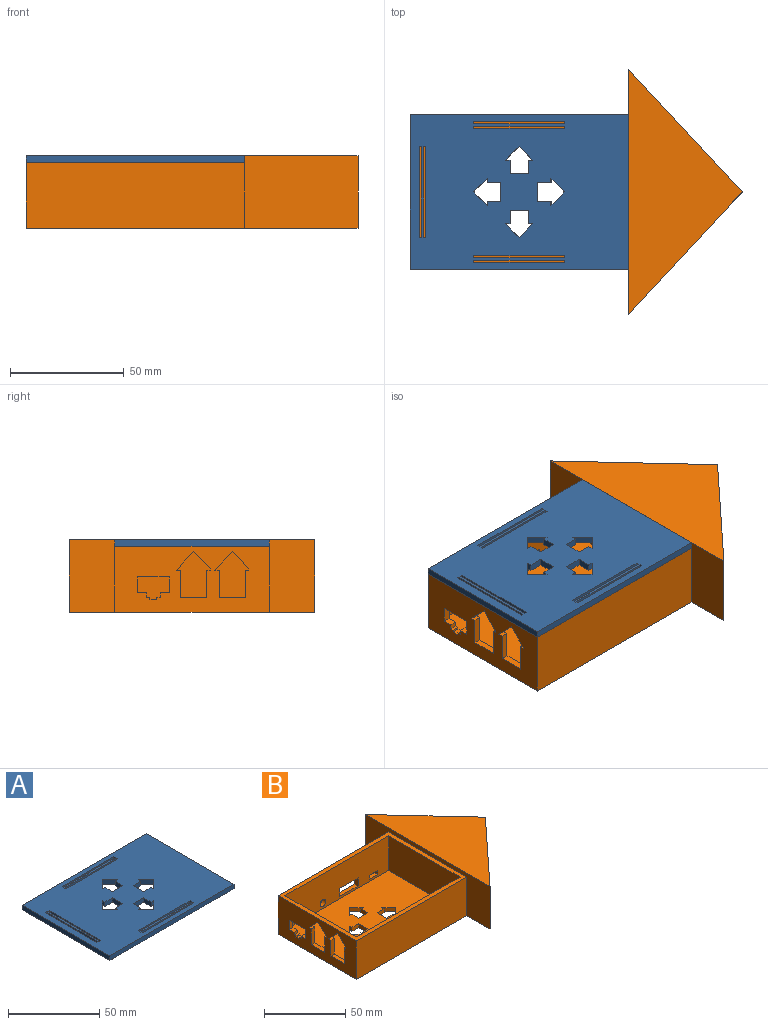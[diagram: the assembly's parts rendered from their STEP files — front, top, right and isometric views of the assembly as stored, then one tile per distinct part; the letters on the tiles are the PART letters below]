
ASSEMBLY  parts=2 mates=1
PART A: 86 faces, bbox 96x68x6 mm
  f0: plane 96x68mm, normal (0,0,-1), area 5872mm2, adj f2,f3,f4,f5,f6,f7,f8,f9
  f1: plane 96x68mm, normal (0,0,1), area 5952mm2, adj f2,f3,f4,f5,f34,f35,f36,f37
  f2: plane 68x3mm, normal (-1,0,0), area 204mm2, adj f0,f1,f3,f5
  f3: plane 96x3mm, normal (0,-1,0), area 288mm2, adj f0,f1,f2,f4
  f4: plane 68x3mm, normal (1,0,0), area 204mm2, adj f0,f1,f3,f5
  f5: plane 96x3mm, normal (0,1,0), area 288mm2, adj f0,f1,f2,f4
  f6: plane 6x3mm, normal (1,0,0), area 18mm2, adj f0,f7,f11,f12
  f7: plane 6x3mm, normal (0,-1,0), area 18mm2, adj f0,f6,f8,f12
  f8: plane 3x2mm, normal (-1,0,0), area 6mm2, adj f0,f7,f9,f12
  f9: plane 4x3mm, normal (0,1,0), area 12mm2, adj f0,f8,f10,f12
  f10: plane 4x3mm, normal (-1,0,0), area 12mm2, adj f0,f9,f11,f12
  f11: plane 3x2mm, normal (0,1,0), area 6mm2, adj f0,f6,f10,f12
  f12: plane 6x6mm, normal (0,0,-1), area 20mm2, adj f6,f7,f8,f9,f10,f11
  f13: plane 6x3mm, normal (1,0,0), area 18mm2, adj f0,f14,f18,f19
  f14: plane 3x2mm, normal (0,-1,0), area 6mm2, adj f0,f13,f15,f19
  f15: plane 4x3mm, normal (-1,0,0), area 12mm2, adj f0,f14,f16,f19
  f16: plane 4x3mm, normal (0,-1,0), area 12mm2, adj f0,f15,f17,f19
  f17: plane 3x2mm, normal (-1,0,0), area 6mm2, adj f0,f16,f18,f19
  f18: plane 6x3mm, normal (0,1,0), area 18mm2, adj f0,f13,f17,f19
  f19: plane 6x6mm, normal (0,0,-1), area 20mm2, adj f13,f14,f15,f16,f17,f18
  f20: plane 6x3mm, normal (0,-1,0), area 18mm2, adj f0,f21,f25,f26
  f21: plane 6x3mm, normal (-1,0,0), area 18mm2, adj f0,f20,f22,f26
  f22: plane 3x2mm, normal (0,1,0), area 6mm2, adj f0,f21,f23,f26
  f23: plane 4x3mm, normal (1,0,0), area 12mm2, adj f0,f22,f24,f26
  f24: plane 4x3mm, normal (0,1,0), area 12mm2, adj f0,f23,f25,f26
  f25: plane 3x2mm, normal (1,0,0), area 6mm2, adj f0,f20,f24,f26
  f26: plane 6x6mm, normal (0,0,-1), area 20mm2, adj f20,f21,f22,f23,f24,f25
  f27: plane 3x2mm, normal (0,-1,0), area 6mm2, adj f0,f28,f32,f33
  f28: plane 6x3mm, normal (-1,0,0), area 18mm2, adj f0,f27,f29,f33
  f29: plane 6x3mm, normal (0,1,0), area 18mm2, adj f0,f28,f30,f33
  f30: plane 3x2mm, normal (1,0,0), area 6mm2, adj f0,f29,f31,f33
  f31: plane 4x3mm, normal (0,-1,0), area 12mm2, adj f0,f30,f32,f33
  f32: plane 4x3mm, normal (1,0,0), area 12mm2, adj f0,f27,f31,f33
  f33: plane 6x6mm, normal (0,0,-1), area 20mm2, adj f27,f28,f29,f30,f31,f32
  f34: plane 8x3mm, normal (1,0,0), area 24mm2, adj f0,f1,f35,f40
  f35: plane 6x3mm, normal (0,1,0), area 18mm2, adj f0,f1,f34,f36
  f36: plane 3x2mm, normal (1,0,0), area 6mm2, adj f0,f1,f35,f37
  f37: plane 6x6mm, normal (-0.71,0.71,0), area 25.5mm2, adj f0,f1,f36,f38
  f38: plane 6x6mm, normal (-0.71,-0.71,0), area 25.5mm2, adj f0,f1,f37,f39
  f39: plane 3x2mm, normal (1,0,0), area 6mm2, adj f0,f1,f38,f40
  f40: plane 6x3mm, normal (0,-1,0), area 18mm2, adj f0,f1,f34,f39
  f41: plane 40x3mm, normal (0,1,0), area 120mm2, adj f0,f1,f42,f44
  f42: plane 3x1mm, normal (-1,0,0), area 3mm2, adj f0,f1,f41,f43
  f43: plane 40x3mm, normal (0,-1,0), area 120mm2, adj f0,f1,f42,f44
  f44: plane 3x1mm, normal (1,0,0), area 3mm2, adj f0,f1,f41,f43
  f45: plane 8x3mm, normal (0,-1,0), area 24mm2, adj f0,f1,f46,f51
  f46: plane 6x3mm, normal (1,0,0), area 18mm2, adj f0,f1,f45,f47
  f47: plane 3x2mm, normal (0,-1,0), area 6mm2, adj f0,f1,f46,f48
  f48: plane 6x6mm, normal (0.71,0.71,0), area 25.5mm2, adj f0,f1,f47,f49
  f49: plane 6x6mm, normal (-0.71,0.71,0), area 25.5mm2, adj f0,f1,f48,f50
  f50: plane 3x2mm, normal (0,-1,0), area 6mm2, adj f0,f1,f49,f51
  f51: plane 6x3mm, normal (-1,0,0), area 18mm2, adj f0,f1,f45,f50
  f52: plane 8x3mm, normal (-1,0,0), area 24mm2, adj f0,f1,f53,f58
  f53: plane 6x3mm, normal (0,-1,0), area 18mm2, adj f0,f1,f52,f54
  f54: plane 3x2mm, normal (-1,0,0), area 6mm2, adj f0,f1,f53,f55
  f55: plane 6x6mm, normal (0.71,-0.71,0), area 25.5mm2, adj f0,f1,f54,f56
  f56: plane 6x6mm, normal (0.71,0.71,0), area 25.5mm2, adj f0,f1,f55,f57
  f57: plane 3x2mm, normal (-1,0,0), area 6mm2, adj f0,f1,f56,f58
  f58: plane 6x3mm, normal (0,1,0), area 18mm2, adj f0,f1,f52,f57
  f59: plane 40x3mm, normal (1,0,0), area 120mm2, adj f0,f1,f60,f62
  f60: plane 3x1mm, normal (0,1,0), area 3mm2, adj f0,f1,f59,f61
  f61: plane 40x3mm, normal (-1,0,0), area 120mm2, adj f0,f1,f60,f62
  f62: plane 3x1mm, normal (0,-1,0), area 3mm2, adj f0,f1,f59,f61
  f63: plane 3x1mm, normal (0,1,0), area 3mm2, adj f0,f1,f64,f66
  f64: plane 40x3mm, normal (-1,0,0), area 120mm2, adj f0,f1,f63,f65
  f65: plane 3x1mm, normal (0,-1,0), area 3mm2, adj f0,f1,f64,f66
  f66: plane 40x3mm, normal (1,0,0), area 120mm2, adj f0,f1,f63,f65
  f67: plane 40x3mm, normal (0,-1,0), area 120mm2, adj f0,f1,f68,f70
  f68: plane 3x1mm, normal (1,0,0), area 3mm2, adj f0,f1,f67,f69
  f69: plane 40x3mm, normal (0,1,0), area 120mm2, adj f0,f1,f68,f70
  f70: plane 3x1mm, normal (-1,0,0), area 3mm2, adj f0,f1,f67,f69
  f71: plane 3x1mm, normal (-1,0,0), area 3mm2, adj f0,f1,f72,f74
  f72: plane 40x3mm, normal (0,-1,0), area 120mm2, adj f0,f1,f71,f73
  f73: plane 3x1mm, normal (1,0,0), area 3mm2, adj f0,f1,f72,f74
  f74: plane 40x3mm, normal (0,1,0), area 120mm2, adj f0,f1,f71,f73
  f75: plane 8x3mm, normal (0,1,0), area 24mm2, adj f0,f1,f76,f81
  f76: plane 6x3mm, normal (-1,0,0), area 18mm2, adj f0,f1,f75,f77
  f77: plane 3x2mm, normal (0,1,0), area 6mm2, adj f0,f1,f76,f78
  f78: plane 6x6mm, normal (-0.71,-0.71,0), area 25.5mm2, adj f0,f1,f77,f79
  f79: plane 6x6mm, normal (0.71,-0.71,0), area 25.5mm2, adj f0,f1,f78,f80
  f80: plane 3x2mm, normal (0,1,0), area 6mm2, adj f0,f1,f79,f81
  f81: plane 6x3mm, normal (1,0,0), area 18mm2, adj f0,f1,f75,f80
  f82: plane 3x1mm, normal (1,0,0), area 3mm2, adj f0,f1,f83,f85
  f83: plane 40x3mm, normal (0,1,0), area 120mm2, adj f0,f1,f82,f84
  f84: plane 3x1mm, normal (-1,0,0), area 3mm2, adj f0,f1,f83,f85
  f85: plane 40x3mm, normal (0,-1,0), area 120mm2, adj f0,f1,f82,f84
PART B: 79 faces, bbox 146x108x32 mm
  f0: plane 146x108mm, normal (0,0,-1), area 8892mm2, adj f1,f3,f5,f47,f48,f49,f51,f52
  f1: plane 96x29mm, normal (0,1,0), area 2647.4mm2, adj f0,f3,f8,f38,f39,f40,f41,f42
  f2: plane 90x26mm, normal (0,-1,0), area 2203.4mm2, adj f4,f6,f8,f9,f38,f39,f40,f41
  f3: plane 68x29mm, normal (-1,0,0), area 1459.3mm2, adj f0,f1,f5,f8,f10,f11,f12,f13
  f4: plane 62x26mm, normal (1,0,0), area 1099.3mm2, adj f2,f7,f8,f9,f10,f11,f12,f13
  f5: plane 96x29mm, normal (0,-1,0), area 2784mm2, adj f0,f3,f8,f47
  f6: plane 62x26mm, normal (-1,0,0), area 1612mm2, adj f2,f7,f8,f9
  f7: plane 90x26mm, normal (0,1,0), area 2340mm2, adj f4,f6,f8,f9
  f8: plane 96x68mm, normal (0,0,1), area 948mm2, adj f1,f2,f3,f4,f5,f6,f7,f47
  f9: plane 90x62mm, normal (0,0,1), area 5244mm2, adj f2,f4,f6,f7,f51,f52,f53,f54
  f10: plane 7.48x7.25mm, normal (0,0.72,-0.7), area 31.3mm2, adj f3,f4,f11,f17
  f11: plane 8x7.75mm, normal (0,-0.72,-0.7), area 33.4mm2, adj f3,f4,f10,f12
  f12: plane 3x2mm, normal (0,0,1), area 6mm2, adj f3,f4,f11,f13
  f13: plane 12x3mm, normal (0,-1,0), area 36mm2, adj f3,f4,f12,f14
  f14: plane 11.5x3mm, normal (0,0,1), area 34.5mm2, adj f3,f4,f13,f15
  f15: plane 12x3mm, normal (0,1,0), area 36mm2, adj f3,f4,f14,f16
  f16: plane 3x1.5mm, normal (0,0,1), area 4.5mm2, adj f3,f4,f15,f17
  f17: plane 3x0.52mm, normal (0,1,0), area 1.5mm2, adj f3,f4,f10,f16
  f18: plane 12x3mm, normal (0,1,0), area 36mm2, adj f3,f4,f19,f25
  f19: plane 3x1.5mm, normal (0,0,1), area 4.5mm2, adj f3,f4,f18,f20
  f20: plane 3x0.52mm, normal (0,1,0), area 1.5mm2, adj f3,f4,f19,f21
  f21: plane 7.48x7.25mm, normal (0,0.72,-0.7), area 31.3mm2, adj f3,f4,f20,f22
  f22: plane 8x7.75mm, normal (0,-0.72,-0.7), area 33.4mm2, adj f3,f4,f21,f23
  f23: plane 3x2mm, normal (0,0,1), area 6mm2, adj f3,f4,f22,f24
  f24: plane 12x3mm, normal (0,-1,0), area 36mm2, adj f3,f4,f23,f25
  f25: plane 11.5x3mm, normal (0,0,1), area 34.5mm2, adj f3,f4,f18,f24
  f26: plane 7x3mm, normal (0,1,0), area 21mm2, adj f3,f4,f27,f37
  f27: plane 14x3mm, normal (0,0,-1), area 42mm2, adj f3,f4,f26,f28
  f28: plane 7x3mm, normal (0,-1,0), area 21mm2, adj f3,f4,f27,f29
  f29: plane 4x3mm, normal (0,0,1), area 12mm2, adj f3,f4,f28,f30
  f30: plane 3x2mm, normal (0,-1,0), area 6mm2, adj f3,f4,f29,f31
  f31: plane 3x1.5mm, normal (0,0,1), area 4.5mm2, adj f3,f4,f30,f32
  f32: plane 3x1mm, normal (0,-1,0), area 3mm2, adj f3,f4,f31,f33
  f33: plane 3x3mm, normal (0,0,1), area 9mm2, adj f3,f4,f32,f34
  f34: plane 3x1mm, normal (0,1,0), area 3mm2, adj f3,f4,f33,f35
  f35: plane 3x1.5mm, normal (0,0,1), area 4.5mm2, adj f3,f4,f34,f36
  f36: plane 3x2mm, normal (0,1,0), area 6mm2, adj f3,f4,f35,f37
  f37: plane 4x3mm, normal (0,0,1), area 12mm2, adj f3,f4,f26,f36
  f38: cylinder r=2.5mm len=5mm, axis (0,1,0), area 47.1mm2, adj f1,f2
  f39: plane 16x3mm, normal (0,0,1), area 48mm2, adj f1,f2,f40,f42
  f40: plane 6x3mm, normal (1,0,0), area 18mm2, adj f1,f2,f39,f41
  f41: plane 16x3mm, normal (0,0,-1), area 48mm2, adj f1,f2,f40,f42
  f42: plane 6x3mm, normal (-1,0,0), area 18mm2, adj f1,f2,f39,f41
  f43: plane 7x3mm, normal (0,0,1), area 21mm2, adj f1,f2,f44,f46
  f44: plane 3x3mm, normal (1,0,0), area 9mm2, adj f1,f2,f43,f45
  f45: plane 7x3mm, normal (0,0,-1), area 21mm2, adj f1,f2,f44,f46
  f46: plane 3x3mm, normal (-1,0,0), area 9mm2, adj f1,f2,f43,f45
  f47: plane 108x32mm, normal (-1,0,0), area 1484mm2, adj f0,f1,f5,f8,f48,f49,f50
  f48: plane 54x50mm, normal (0.73,-0.68,0), area 2355mm2, adj f0,f47,f49,f50
  f49: plane 54x50mm, normal (0.73,0.68,0), area 2355mm2, adj f0,f47,f48,f50
  f50: plane 108x50mm, normal (0,0,1), area 2700mm2, adj f47,f48,f49
  f51: plane 8x3mm, normal (0,1,0), area 24mm2, adj f0,f9,f52,f57
  f52: plane 6x3mm, normal (1,0,0), area 18mm2, adj f0,f9,f51,f53
  f53: plane 3x2mm, normal (0,1,0), area 6mm2, adj f0,f9,f52,f54
  f54: plane 6x6mm, normal (0.71,-0.71,0), area 25.5mm2, adj f0,f9,f53,f55
  f55: plane 6x6mm, normal (-0.71,-0.71,0), area 25.5mm2, adj f0,f9,f54,f56
  f56: plane 3x2mm, normal (0,1,0), area 6mm2, adj f0,f9,f55,f57
  f57: plane 6x3mm, normal (-1,0,0), area 18mm2, adj f0,f9,f51,f56
  f58: plane 8x3mm, normal (1,0,0), area 24mm2, adj f0,f9,f59,f64
  f59: plane 6x3mm, normal (0,-1,0), area 18mm2, adj f0,f9,f58,f60
  f60: plane 3x2mm, normal (1,0,0), area 6mm2, adj f0,f9,f59,f61
  f61: plane 6x6mm, normal (-0.71,-0.71,0), area 25.5mm2, adj f0,f9,f60,f62
  f62: plane 6x6mm, normal (-0.71,0.71,0), area 25.5mm2, adj f0,f9,f61,f63
  f63: plane 3x2mm, normal (1,0,0), area 6mm2, adj f0,f9,f62,f64
  f64: plane 6x3mm, normal (0,1,0), area 18mm2, adj f0,f9,f58,f63
  f65: plane 8x3mm, normal (0,-1,0), area 24mm2, adj f0,f9,f66,f71
  f66: plane 6x3mm, normal (-1,0,0), area 18mm2, adj f0,f9,f65,f67
  f67: plane 3x2mm, normal (0,-1,0), area 6mm2, adj f0,f9,f66,f68
  f68: plane 6x6mm, normal (-0.71,0.71,0), area 25.5mm2, adj f0,f9,f67,f69
  f69: plane 6x6mm, normal (0.71,0.71,0), area 25.5mm2, adj f0,f9,f68,f70
  f70: plane 3x2mm, normal (0,-1,0), area 6mm2, adj f0,f9,f69,f71
  f71: plane 6x3mm, normal (1,0,0), area 18mm2, adj f0,f9,f65,f70
  f72: plane 8x3mm, normal (-1,0,0), area 24mm2, adj f0,f9,f73,f78
  f73: plane 6x3mm, normal (0,1,0), area 18mm2, adj f0,f9,f72,f74
  f74: plane 3x2mm, normal (-1,0,0), area 6mm2, adj f0,f9,f73,f75
  f75: plane 6x6mm, normal (0.71,0.71,0), area 25.5mm2, adj f0,f9,f74,f76
  f76: plane 6x6mm, normal (0.71,-0.71,0), area 25.5mm2, adj f0,f9,f75,f77
  f77: plane 3x2mm, normal (-1,0,0), area 6mm2, adj f0,f9,f76,f78
  f78: plane 6x3mm, normal (0,-1,0), area 18mm2, adj f0,f9,f72,f77
PLACE A t=(-113.69,-75.96,34.82)mm
PLACE B t=(-65.61,-41.96,5.82)mm
MATE fastened A.f0 <-> B.f8  axis (0,0,-1) through (-65.11,-41.96,31.82)mm
